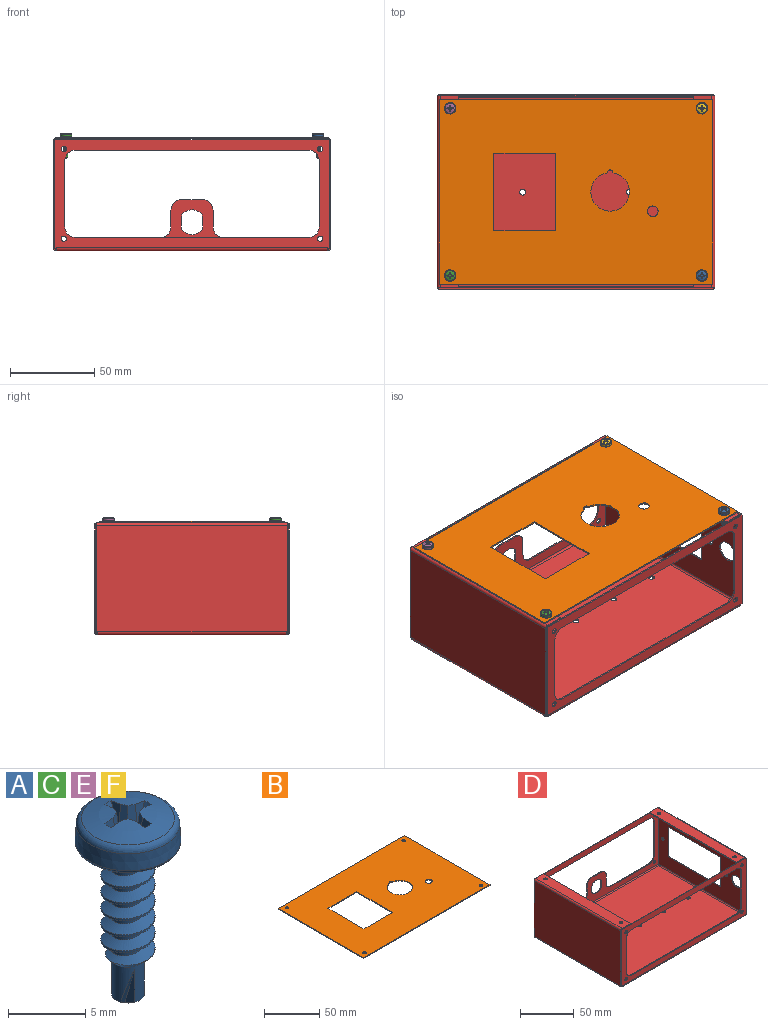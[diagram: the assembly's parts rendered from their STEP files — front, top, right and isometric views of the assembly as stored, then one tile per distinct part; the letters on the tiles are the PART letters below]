
ASSEMBLY  parts=6 mates=10
PART A: 60 faces, bbox 7.8x7.8x15.5 mm
  f0: cylinder r=1.75mm len=3.51mm, axis (0,0,1), area 0.9mm2, adj f8,f9,f30,f32
  f1: cylinder r=1.75mm len=3.51mm, axis (0,0,1), area 0.9mm2, adj f9,f10,f30,f32
  f2: cylinder r=1.75mm len=3.51mm, axis (0,0,1), area 0.9mm2, adj f10,f11,f30,f32
  f3: cylinder r=1.75mm len=3.51mm, axis (0,0,1), area 0.9mm2, adj f11,f12,f30,f32
  f4: cylinder r=1.75mm len=3.51mm, axis (0,0,1), area 0.9mm2, adj f12,f13,f30,f32
  f5: cylinder r=1.75mm len=3.51mm, axis (0,0,1), area 0.9mm2, adj f13,f30,f31,f32
  f6: cylinder r=1.75mm len=0.2mm, axis (0,0,1), area 0mm2, adj f31,f32,f33
  f7: cylinder r=1.75mm len=1.75mm, axis (0,0,1), area 0.3mm2, adj f8,f17,f30,f32
  f8: cylinder r=1.75mm len=3.51mm, axis (0,0,1), area 0.9mm2, adj f0,f7,f30,f32
  f9: cylinder r=1.75mm len=3.51mm, axis (0,0,1), area 0.9mm2, adj f0,f1,f30,f32
  f10: cylinder r=1.75mm len=3.51mm, axis (0,0,1), area 0.9mm2, adj f1,f2,f30,f32
  f11: cylinder r=1.75mm len=3.51mm, axis (0,0,1), area 0.9mm2, adj f2,f3,f30,f32
  f12: cylinder r=1.75mm len=3.51mm, axis (0,0,1), area 0.9mm2, adj f3,f4,f30,f32
  f13: cylinder r=1.75mm len=3.51mm, axis (0,0,1), area 0.9mm2, adj f4,f5,f30,f32
  f14: torus R=3.23mm, axis (0,0,-1), area 7mm2, adj f16,f17
  f15: sphere r=9.5mm, area 24.2mm2, adj f38,f39,f40,f41,f42,f43,f44,f46
  f16: cone r=3.34mm half-angle=3deg, axis (0,0,-1), area 27.8mm2, adj f14,f38
  f17: plane 6.79x6.79mm, normal (0,0,-1), area 26.6mm2, adj f7,f14,f24,f25,f30,f32
  f18: cylinder r=1.06mm len=2.12mm, axis (0,0,1), area 2.1mm2, adj f19,f26,f28,f30,f32
  f19: cylinder r=1.06mm len=2.12mm, axis (0,0,1), area 2.1mm2, adj f18,f20,f30,f32
  f20: cylinder r=1.06mm len=2.12mm, axis (0,0,1), area 2.1mm2, adj f19,f21,f30,f32
  f21: cylinder r=1.06mm len=2.12mm, axis (0,0,1), area 2.1mm2, adj f20,f22,f30,f32
  f22: cylinder r=1.06mm len=2.12mm, axis (0,0,1), area 2.1mm2, adj f21,f23,f30,f32
  f23: cylinder r=1.06mm len=2.12mm, axis (0,0,1), area 2.1mm2, adj f22,f24,f30,f32
  f24: cylinder r=1.06mm len=2.12mm, axis (0,0,1), area 2mm2, adj f17,f23,f25,f30,f32
  f25: cylinder r=1.06mm len=0.55mm, axis (0,0,1), area 0mm2, adj f17,f24,f32
  f26: cylinder r=1.06mm len=3.27mm, axis (0,0,1), area 16.7mm2, adj f18,f27,f29,f30,f33,f34,f35,f36
  f27: cone r=0mm half-angle=55deg, axis (0,0,1), area 3.7mm2, adj f26,f34,f35,f36,f37
  f28: cone r=1.24mm half-angle=60deg, axis (0,0,-1), area 0.5mm2, adj f18,f29,f32,f33
  f29: cylinder r=1.24mm len=0.17mm, axis (0,0,1), area 0mm2, adj f26,f28,f33
  f30: bspline ~9.71x4.05mm, area 49.1mm2, adj f0,f1,f2,f3,f4,f5,f7,f8
  f31: cylinder r=1.75mm len=3.51mm, axis (0,0,1), area 0.8mm2, adj f5,f6,f30,f32,f33
  f32: bspline ~9.5x4.05mm, area 48.6mm2, adj f0,f1,f2,f3,f4,f5,f6,f7
  f33: cone r=6.06mm half-angle=45deg, axis (0,0,1), area 3.5mm2, adj f6,f26,f28,f29,f30,f31,f32
  f34: plane 3.1x0.95mm, normal (-0.17,0.94,-0.28), area 1.2mm2, adj f26,f27,f35
  f35: plane 3.45x1.3mm, normal (1,0,0), area 1.2mm2, adj f26,f27,f34
  f36: plane 3.1x0.95mm, normal (0.17,-0.94,-0.28), area 1.2mm2, adj f26,f27,f37
  f37: plane 3.45x1.3mm, normal (-1,0,0), area 1.2mm2, adj f26,f27,f36
  f38: torus R=2.85mm, axis (0,0,-1), area 12.3mm2, adj f15,f16
  f39: cone r=2.03mm half-angle=22deg, axis (0,0,1), area 0.8mm2, adj f15,f40,f45,f59
  f40: plane 1.77x0.91mm, normal (-0.99,0,0.1), area 0.9mm2, adj f15,f39,f41,f45
  f41: plane 1.84x0.71mm, normal (-0.92,-0.38,0.1), area 1mm2, adj f15,f40,f42,f45
  f42: plane 1.84x0.71mm, normal (-0.38,-0.92,0.1), area 1mm2, adj f15,f41,f43,f45
  f43: plane 1.77x0.91mm, normal (0,-0.99,0.1), area 0.9mm2, adj f15,f42,f44,f45
  f44: cone r=2.03mm half-angle=22deg, axis (0,0,1), area 0.8mm2, adj f15,f43,f45,f46
  f45: plane 2.42x2.42mm, normal (0,0,1), area 2.1mm2, adj f39,f40,f41,f42,f43,f44,f46,f47
  f46: plane 1.77x0.91mm, normal (0,0.99,0.1), area 0.9mm2, adj f15,f44,f45,f47
  f47: plane 1.84x0.71mm, normal (-0.38,0.92,0.1), area 1mm2, adj f15,f45,f46,f48
  f48: plane 1.84x0.71mm, normal (-0.92,0.38,0.1), area 1mm2, adj f15,f45,f47,f49
  f49: plane 1.77x0.91mm, normal (-0.99,0,0.1), area 0.9mm2, adj f15,f45,f48,f50
  f50: cone r=2.03mm half-angle=22deg, axis (0,0,1), area 0.8mm2, adj f15,f45,f49,f51
  f51: plane 1.77x0.91mm, normal (0.99,0,0.1), area 0.9mm2, adj f15,f45,f50,f52
  f52: plane 1.84x0.71mm, normal (0.92,0.38,0.1), area 1mm2, adj f15,f45,f51,f53
  f53: plane 1.84x0.71mm, normal (0.38,0.92,0.1), area 1mm2, adj f15,f45,f52,f54
  f54: plane 1.77x0.91mm, normal (0,0.99,0.1), area 0.9mm2, adj f15,f45,f53,f55
  f55: cone r=2.03mm half-angle=22deg, axis (0,0,1), area 0.8mm2, adj f15,f45,f54,f56
  f56: plane 1.77x0.91mm, normal (0,-0.99,0.1), area 0.9mm2, adj f15,f45,f55,f57
  f57: plane 1.84x0.71mm, normal (0.38,-0.92,0.1), area 1mm2, adj f15,f45,f56,f58
  f58: plane 1.84x0.71mm, normal (0.92,-0.38,0.1), area 1mm2, adj f15,f45,f57,f59
  f59: plane 1.77x0.91mm, normal (0.99,0,0.1), area 0.9mm2, adj f15,f39,f45,f58
PART B: 17 faces, bbox 162.6x109.7x0.8 mm
  f0: plane 162.56x0.81mm, normal (0,-1,0), area 132.1mm2, adj f1,f14,f15,f16
  f1: plane 109.73x0.81mm, normal (-1,0,0), area 89.2mm2, adj f0,f2,f15,f16
  f2: plane 162.56x0.81mm, normal (0,1,0), area 132.1mm2, adj f1,f14,f15,f16
  f3: cylinder r=11.43mm len=22.86mm, axis (0,0,1), area 55.7mm2, adj f13,f15,f16
  f4: plane 36.83x0.81mm, normal (0,1,0), area 29.9mm2, adj f5,f12,f15,f16
  f5: plane 46.23x0.81mm, normal (-1,0,0), area 37.6mm2, adj f4,f6,f15,f16
  f6: plane 36.83x0.81mm, normal (0,-1,0), area 29.9mm2, adj f5,f12,f15,f16
  f7: cylinder r=3.17mm len=6.35mm, axis (0,0,1), area 16.2mm2, adj f15,f16
  f8: cylinder r=1.59mm len=3.18mm, axis (0,0,1), area 8.1mm2, adj f15,f16
  f9: cylinder r=1.59mm len=3.18mm, axis (0,0,1), area 8.1mm2, adj f15,f16
  f10: cylinder r=1.59mm len=3.18mm, axis (0,0,1), area 8.1mm2, adj f15,f16
  f11: cylinder r=1.59mm len=3.18mm, axis (0,0,1), area 8.1mm2, adj f15,f16
  f12: plane 46.23x0.81mm, normal (1,0,0), area 37.6mm2, adj f4,f6,f15,f16
  f13: cylinder r=1.65mm len=3.3mm, axis (0,0,1), area 4.4mm2, adj f3,f15,f16
  f14: plane 109.73x0.81mm, normal (1,0,0), area 89.2mm2, adj f0,f2,f15,f16
  f15: plane 162.56x109.73mm, normal (0,0,-1), area 15656.6mm2, adj f0,f1,f2,f3,f4,f5,f6,f7
  f16: plane 162.56x109.73mm, normal (0,0,1), area 15656.6mm2, adj f0,f1,f2,f3,f4,f5,f6,f7
PART C: same geometry as A
PART D: 114 faces, bbox 165.2x115.9x66.8 mm
  f0: plane 0.97x0.81mm, normal (0,0,-1), area 0.8mm2, adj f20,f29,f30,f38
  f1: plane 9.93x0.81mm, normal (-1,0,0), area 8.1mm2, adj f2,f28,f29,f30
  f2: cylinder r=6.35mm len=6.35mm, axis (0,1,0), area 8.1mm2, adj f1,f3,f29,f30
  f3: plane 12.34x0.81mm, normal (0,0,1), area 10mm2, adj f2,f4,f29,f30
  f4: cylinder r=6.35mm len=6.35mm, axis (0,1,0), area 8.1mm2, adj f3,f5,f29,f30
  f5: plane 9.93x0.81mm, normal (1,0,0), area 8.1mm2, adj f4,f6,f29,f30
  f6: cylinder r=6.35mm len=6.35mm, axis (0,1,0), area 8.1mm2, adj f5,f7,f29,f30
  f7: plane 50.47x0.81mm, normal (0,0,1), area 41mm2, adj f6,f8,f29,f30
  f8: cylinder r=6.35mm len=6.35mm, axis (0,1,0), area 8.1mm2, adj f7,f9,f29,f30
  f9: plane 39.37x0.81mm, normal (-1,0,0), area 32mm2, adj f8,f10,f29,f30
  f10: cylinder r=6.35mm len=6.35mm, axis (0,1,0), area 8.1mm2, adj f9,f11,f29,f30
  f11: plane 138.68x0.81mm, normal (0,0,-1), area 112.7mm2, adj f10,f12,f29,f30
  f12: cylinder r=6.35mm len=6.35mm, axis (0,1,0), area 8.1mm2, adj f11,f13,f29,f30
  f13: plane 39.37x0.81mm, normal (1,0,0), area 32mm2, adj f12,f14,f29,f30
  f14: cylinder r=6.35mm len=6.35mm, axis (0,1,0), area 8.1mm2, adj f13,f15,f29,f30
  f15: plane 50.47x0.81mm, normal (0,0,1), area 41mm2, adj f14,f28,f29,f30
  f16: plane 7.11x0.81mm, normal (1,0,0), area 5.8mm2, adj f17,f27,f29,f30
  f17: cylinder r=7.37mm len=12.9mm, axis (0,1,0), area 12.8mm2, adj f16,f18,f29,f30
  f18: plane 7.11x0.81mm, normal (-1,0,0), area 5.8mm2, adj f17,f27,f29,f30
  f19: plane 163.53x0.81mm, normal (0,0,1), area 132.9mm2, adj f20,f26,f29,f30
  f20: plane 64.21x0.81mm, normal (1,0,0), area 52.2mm2, adj f0,f19,f29,f30
  f21: plane 0.97x0.81mm, normal (0,0,-1), area 0.8mm2, adj f26,f29,f30,f39
  f22: cylinder r=1.59mm len=3.18mm, axis (0,1,0), area 8.1mm2, adj f29,f30
  f23: cylinder r=1.59mm len=3.18mm, axis (0,1,0), area 8.1mm2, adj f29,f30
  f24: cylinder r=1.59mm len=3.18mm, axis (0,1,0), area 8.1mm2, adj f29,f30
  f25: cylinder r=1.59mm len=3.18mm, axis (0,1,0), area 8.1mm2, adj f29,f30
  f26: plane 64.21x0.81mm, normal (-1,0,0), area 52.2mm2, adj f19,f21,f29,f30
  f27: cylinder r=7.37mm len=12.9mm, axis (0,1,0), area 12.8mm2, adj f16,f18,f29,f30
  f28: cylinder r=6.35mm len=6.35mm, axis (0,1,0), area 8.1mm2, adj f1,f15,f29,f30
  f29: plane 163.53x64.21mm, normal (0,1,0), area 3025.6mm2, adj f0,f1,f2,f3,f4,f5,f6,f7
  f30: plane 163.53x64.21mm, normal (0,-1,0), area 3025.6mm2, adj f0,f1,f2,f3,f4,f5,f6,f7
  f31: cylinder r=1.78mm len=3.56mm, axis (0,0,1), area 9.1mm2, adj f36,f37
  f32: cylinder r=1.78mm len=3.56mm, axis (0,0,1), area 9.1mm2, adj f36,f37
  f33: cylinder r=1.78mm len=3.56mm, axis (0,0,1), area 9.1mm2, adj f36,f37
  f34: cylinder r=1.78mm len=3.56mm, axis (0,0,1), area 9.1mm2, adj f36,f37
  f35: cylinder r=1.78mm len=3.56mm, axis (0,0,1), area 9.1mm2, adj f36,f37
  f36: plane 161.59x112.32mm, normal (0,0,-1), area 18100.5mm2, adj f31,f32,f33,f34,f35,f40,f63,f67
  f37: plane 161.59x112.32mm, normal (0,0,1), area 18100.5mm2, adj f31,f32,f33,f34,f35,f41,f64,f68
  f38: plane 1.8x1.8mm, normal (1,0,0), area 1.8mm2, adj f0,f40,f41,f70
  f39: plane 1.8x1.8mm, normal (-1,0,0), area 1.8mm2, adj f21,f40,f41,f66
  f40: cylinder r=1.8mm len=161.59mm, axis (1,0,0), area 457.8mm2, adj f29,f36,f38,f39
  f41: cylinder r=0.99mm len=161.59mm, axis (1,0,0), area 251.4mm2, adj f30,f37,f38,f39
  f42: plane 0.97x0.81mm, normal (0,0,-1), area 0.8mm2, adj f44,f59,f60,f62
  f43: plane 163.53x0.81mm, normal (0,0,1), area 132.9mm2, adj f44,f58,f59,f60
  f44: plane 64.21x0.81mm, normal (-1,0,0), area 52.2mm2, adj f42,f43,f59,f60
  f45: plane 0.97x0.81mm, normal (0,0,-1), area 0.8mm2, adj f58,f59,f60,f61
  f46: plane 39.37x0.81mm, normal (-1,0,0), area 32mm2, adj f47,f57,f59,f60
  f47: cylinder r=6.35mm len=6.35mm, axis (0,1,0), area 8.1mm2, adj f46,f48,f59,f60
  f48: plane 138.68x0.81mm, normal (0,0,1), area 112.7mm2, adj f47,f49,f59,f60
  f49: cylinder r=6.35mm len=6.35mm, axis (0,1,0), area 8.1mm2, adj f48,f50,f59,f60
  f50: plane 39.37x0.81mm, normal (1,0,0), area 32mm2, adj f49,f51,f59,f60
  f51: cylinder r=6.35mm len=6.35mm, axis (0,1,0), area 8.1mm2, adj f50,f52,f59,f60
  f52: plane 138.68x0.81mm, normal (0,0,-1), area 112.7mm2, adj f51,f57,f59,f60
  f53: cylinder r=1.59mm len=3.18mm, axis (0,1,0), area 8.1mm2, adj f59,f60
  f54: cylinder r=1.59mm len=3.18mm, axis (0,1,0), area 8.1mm2, adj f59,f60
  f55: cylinder r=1.59mm len=3.18mm, axis (0,1,0), area 8.1mm2, adj f59,f60
  f56: cylinder r=1.59mm len=3.18mm, axis (0,1,0), area 8.1mm2, adj f59,f60
  f57: cylinder r=6.35mm len=6.35mm, axis (0,1,0), area 8.1mm2, adj f46,f52,f59,f60
  f58: plane 64.21x0.81mm, normal (1,0,0), area 52.2mm2, adj f43,f45,f59,f60
  f59: plane 163.53x64.21mm, normal (0,-1,0), area 2620.5mm2, adj f42,f43,f44,f45,f46,f47,f48,f49
  f60: plane 163.53x64.21mm, normal (0,1,0), area 2620.5mm2, adj f42,f43,f44,f45,f46,f47,f48,f49
  f61: plane 1.8x1.8mm, normal (1,0,0), area 1.8mm2, adj f45,f63,f64,f69
  f62: plane 1.8x1.8mm, normal (-1,0,0), area 1.8mm2, adj f42,f63,f64,f65
  f63: cylinder r=1.8mm len=161.59mm, axis (1,0,0), area 457.8mm2, adj f36,f59,f61,f62
  f64: cylinder r=0.99mm len=161.59mm, axis (1,0,0), area 251.4mm2, adj f37,f60,f61,f62
  f65: plane 1.8x1.8mm, normal (0,-1,0), area 1.8mm2, adj f62,f67,f68,f99
  f66: plane 1.8x1.8mm, normal (0,1,0), area 1.8mm2, adj f39,f67,f68,f97
  f67: cylinder r=1.8mm len=112.32mm, axis (0,-1,0), area 318.2mm2, adj f36,f65,f66,f101
  f68: cylinder r=0.99mm len=112.32mm, axis (0,-1,0), area 174.8mm2, adj f37,f65,f66,f102
  f69: plane 1.8x1.8mm, normal (0,-1,0), area 1.8mm2, adj f61,f71,f72,f73
  f70: plane 1.8x1.8mm, normal (0,1,0), area 1.8mm2, adj f38,f71,f72,f78
  f71: cylinder r=1.8mm len=112.32mm, axis (0,-1,0), area 318.2mm2, adj f36,f69,f70,f84
  f72: cylinder r=0.99mm len=112.32mm, axis (0,-1,0), area 174.8mm2, adj f37,f69,f70,f85
  f73: plane 0.97x0.81mm, normal (0,0,-1), area 0.8mm2, adj f69,f77,f84,f85
  f74: plane 33.66x0.81mm, normal (0,-1,0), area 27.4mm2, adj f75,f83,f84,f85
  f75: plane 68.58x0.81mm, normal (0,0,1), area 55.7mm2, adj f74,f76,f84,f85
  f76: plane 33.66x0.81mm, normal (0,1,0), area 27.4mm2, adj f75,f83,f84,f85
  f77: plane 63.22x0.81mm, normal (0,-1,0), area 51.4mm2, adj f73,f84,f85,f93
  f78: plane 0.97x0.81mm, normal (0,0,-1), area 0.8mm2, adj f70,f82,f84,f85
  f79: cylinder r=6.25mm len=12.5mm, axis (1,0,0), area 31.9mm2, adj f84,f85
  f80: cylinder r=1.59mm len=3.18mm, axis (1,0,0), area 8.1mm2, adj f84,f85
  f81: cylinder r=1.59mm len=3.18mm, axis (1,0,0), area 8.1mm2, adj f84,f85
  f82: plane 63.22x0.81mm, normal (0,1,0), area 51.4mm2, adj f78,f84,f85,f94
  f83: plane 68.58x0.81mm, normal (0,0,-1), area 55.7mm2, adj f74,f76,f84,f85
  f84: plane 114.25x63.22mm, normal (1,0,0), area 4776.4mm2, adj f71,f73,f74,f75,f76,f77,f78,f79
  f85: plane 114.25x63.22mm, normal (-1,0,0), area 4776.4mm2, adj f72,f73,f74,f75,f76,f77,f78,f79
  f86: plane 114.25x0.81mm, normal (-1,0,0), area 92.9mm2, adj f87,f90,f91,f92
  f87: plane 10.9x0.81mm, normal (0,-1,0), area 8.9mm2, adj f86,f91,f92,f93
  f88: cylinder r=1.59mm len=3.18mm, axis (0,0,1), area 8.1mm2, adj f91,f92
  f89: cylinder r=1.59mm len=3.18mm, axis (0,0,1), area 8.1mm2, adj f91,f92
  f90: plane 10.9x0.81mm, normal (0,1,0), area 8.9mm2, adj f86,f91,f92,f94
  f91: plane 114.25x10.9mm, normal (0,0,1), area 1229.1mm2, adj f86,f87,f88,f89,f90,f95
  f92: plane 114.25x10.9mm, normal (0,0,-1), area 1229.1mm2, adj f86,f87,f88,f89,f90,f96
  f93: plane 1.8x1.8mm, normal (0,-1,0), area 1.8mm2, adj f77,f87,f95,f96
  f94: plane 1.8x1.8mm, normal (0,1,0), area 1.8mm2, adj f82,f90,f95,f96
  f95: cylinder r=1.8mm len=114.25mm, axis (0,-1,0), area 323.6mm2, adj f84,f91,f93,f94
  f96: cylinder r=0.99mm len=114.25mm, axis (0,-1,0), area 177.8mm2, adj f85,f92,f93,f94
  f97: plane 0.97x0.81mm, normal (0,0,-1), area 0.8mm2, adj f66,f98,f101,f102
  f98: plane 63.22x0.81mm, normal (0,1,0), area 51.4mm2, adj f97,f101,f102,f110
  f99: plane 0.97x0.81mm, normal (0,0,-1), area 0.8mm2, adj f65,f100,f101,f102
  f100: plane 63.22x0.81mm, normal (0,-1,0), area 51.4mm2, adj f99,f101,f102,f111
  f101: plane 114.25x63.22mm, normal (-1,0,0), area 7222.9mm2, adj f67,f97,f98,f99,f100,f112
  f102: plane 114.25x63.22mm, normal (1,0,0), area 7222.9mm2, adj f68,f97,f98,f99,f100,f113
  f103: plane 114.25x0.81mm, normal (1,0,0), area 92.9mm2, adj f104,f107,f108,f109
  f104: plane 10.9x0.81mm, normal (0,1,0), area 8.9mm2, adj f103,f108,f109,f110
  f105: cylinder r=1.59mm len=3.18mm, axis (0,0,1), area 8.1mm2, adj f108,f109
  f106: cylinder r=1.59mm len=3.18mm, axis (0,0,1), area 8.1mm2, adj f108,f109
  f107: plane 10.9x0.81mm, normal (0,-1,0), area 8.9mm2, adj f103,f108,f109,f111
  f108: plane 114.25x10.9mm, normal (0,0,1), area 1229.1mm2, adj f103,f104,f105,f106,f107,f112
  f109: plane 114.25x10.9mm, normal (0,0,-1), area 1229.1mm2, adj f103,f104,f105,f106,f107,f113
  f110: plane 1.8x1.8mm, normal (0,1,0), area 1.8mm2, adj f98,f104,f112,f113
  f111: plane 1.8x1.8mm, normal (0,-1,0), area 1.8mm2, adj f100,f107,f112,f113
  f112: cylinder r=1.8mm len=114.25mm, axis (0,1,0), area 323.6mm2, adj f101,f108,f110,f111
  f113: cylinder r=0.99mm len=114.25mm, axis (0,1,0), area 177.8mm2, adj f102,f109,f110,f111
PART E: same geometry as A
PART F: same geometry as A
PLACE A t=(198.08,57.03,73.9)mm
PLACE B t=(41.87,51.95,82.21)mm
PLACE C t=(48.22,57.03,73.9)mm
PLACE D t=(41.36,49.66,16.2)mm fixed
PLACE E t=(48.22,156.59,73.9)mm
PLACE F t=(198.08,156.59,73.9)mm
MATE planar E.f17 <-> B.f16  axis (0,0,-1) through (46.99,157.84,83.03)mm
MATE cylindrical F.f0 <-> B.f10  axis (0,0,1) through (198.08,156.59,71.07)mm
MATE planar F.f17 <-> B.f16  axis (0,0,-1) through (198.16,156.56,83.03)mm
MATE cylindrical A.f0 <-> B.f8  axis (0,0,1) through (198.08,57.03,77.05)mm
MATE cylindrical C.f0 <-> B.f9  axis (0,0,1) through (48.22,57.03,77.05)mm
MATE cylindrical E.f0 <-> B.f11  axis (0,0,1) through (48.22,156.59,77.05)mm
MATE planar A.f17 <-> B.f16  axis (0,0,-1) through (198.16,56.99,83.03)mm
MATE cylindrical C.f0 <-> D.f105  axis (0,0,1) through (48.22,57.03,71.07)mm
MATE planar B.f15 <-> D.f108  axis (0,0,-1) through (125.83,106.83,82.21)mm
MATE planar C.f17 <-> B.f16  axis (0,0,-1) through (48.64,56.06,83.03)mm
